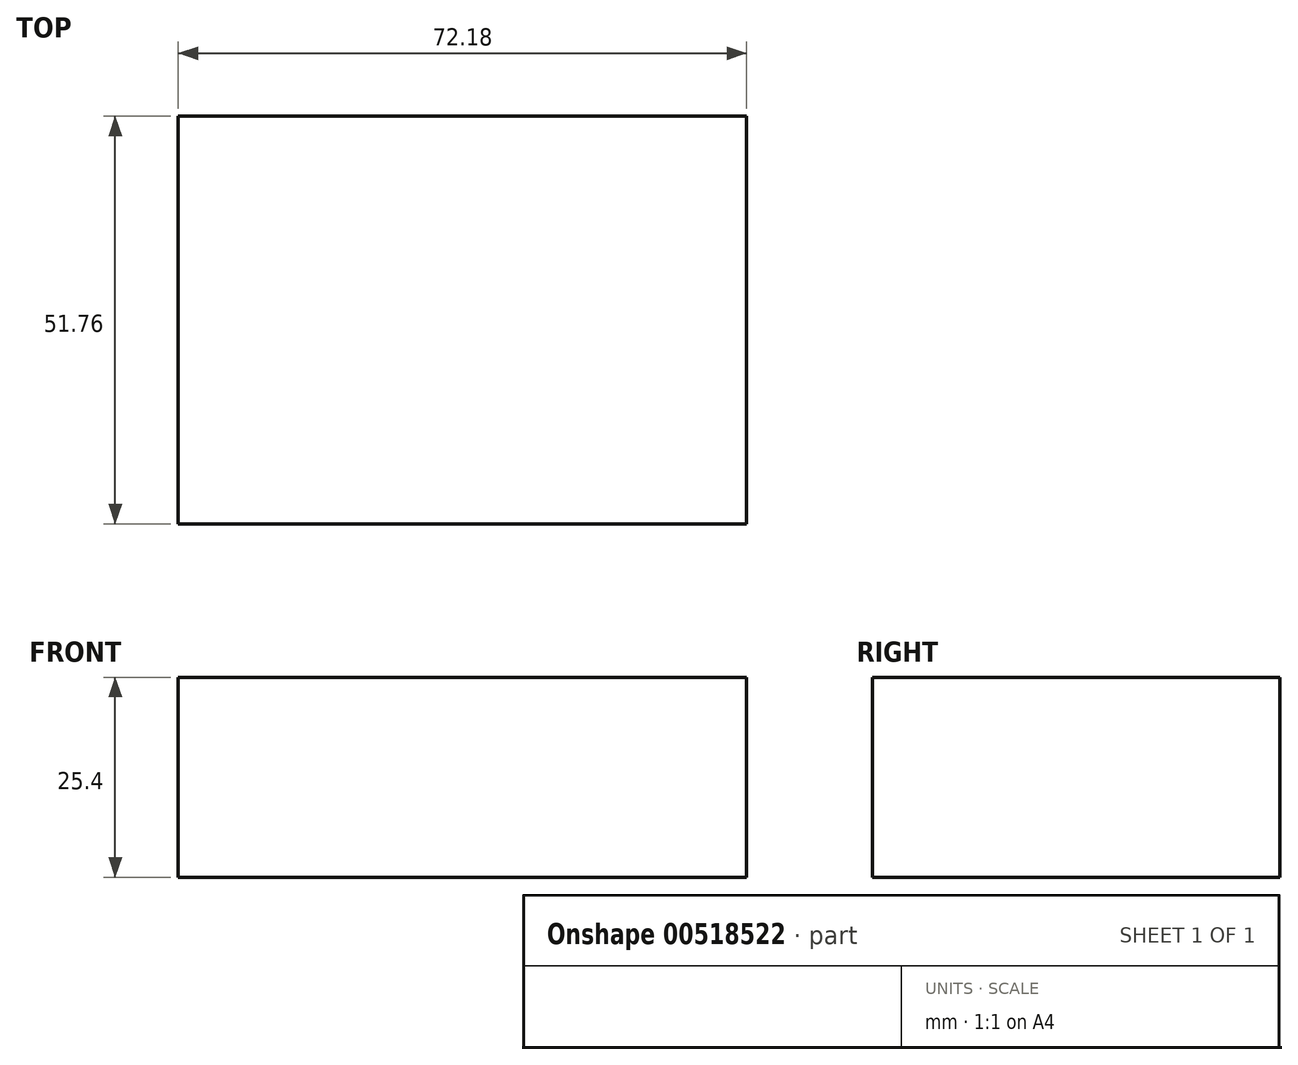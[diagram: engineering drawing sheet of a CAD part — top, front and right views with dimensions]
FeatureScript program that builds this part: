
annotation { "Feature Type Name" : "Feature", "Feature Type Description" : "" }
export const myFeature = defineFeature(function(context is Context, id is Id, definition is map)
    precondition{}
    {
        {
            var Q0;
            Q0=qCreatedBy(makeId("Top.planeOp"),FACE);
            var sketch = newSketch(context, id + "F0", { "sketchPlane" : qUnion([Q0])});
            skLineSegment(sketch, "E0.bottom", {"start": v(36.09, -25.88) * mm, "end": v(-36.09, -25.88) * mm});
            skLineSegment(sketch, "E0.top", {"start": v(36.09, 25.88) * mm, "end": v(-36.09, 25.88) * mm});
            skLineSegment(sketch, "E0.left", {"start": v(36.09, -25.88) * mm, "end": v(36.09, 25.88) * mm});
            skLineSegment(sketch, "E0.right", {"start": v(-36.09, -25.88) * mm, "end": v(-36.09, 25.88) * mm});
            skPoint(sketch, "E0.middle", {"position": v(0, 0) * mm});
            skSolve(sketch);
        }
        {
            var Q0;
            Q0=makeQuery(id+"F0.imprint","IMPRINT",FACE,{"disambiguationData":[TD([[makeQuery(id+"F0.imprint","IMPRINT",EDGE,{"derivedFrom":sQuery(id+"F0.wireOp",EDGE,"E0.bottom")}),-1.0]])]});
            extrude(context, id + "F1", {"entities" : qUnion([Q0]), "depth" : 25.4 * mm, "offsetDistance" : 25.4 * mm});
        }
    });
